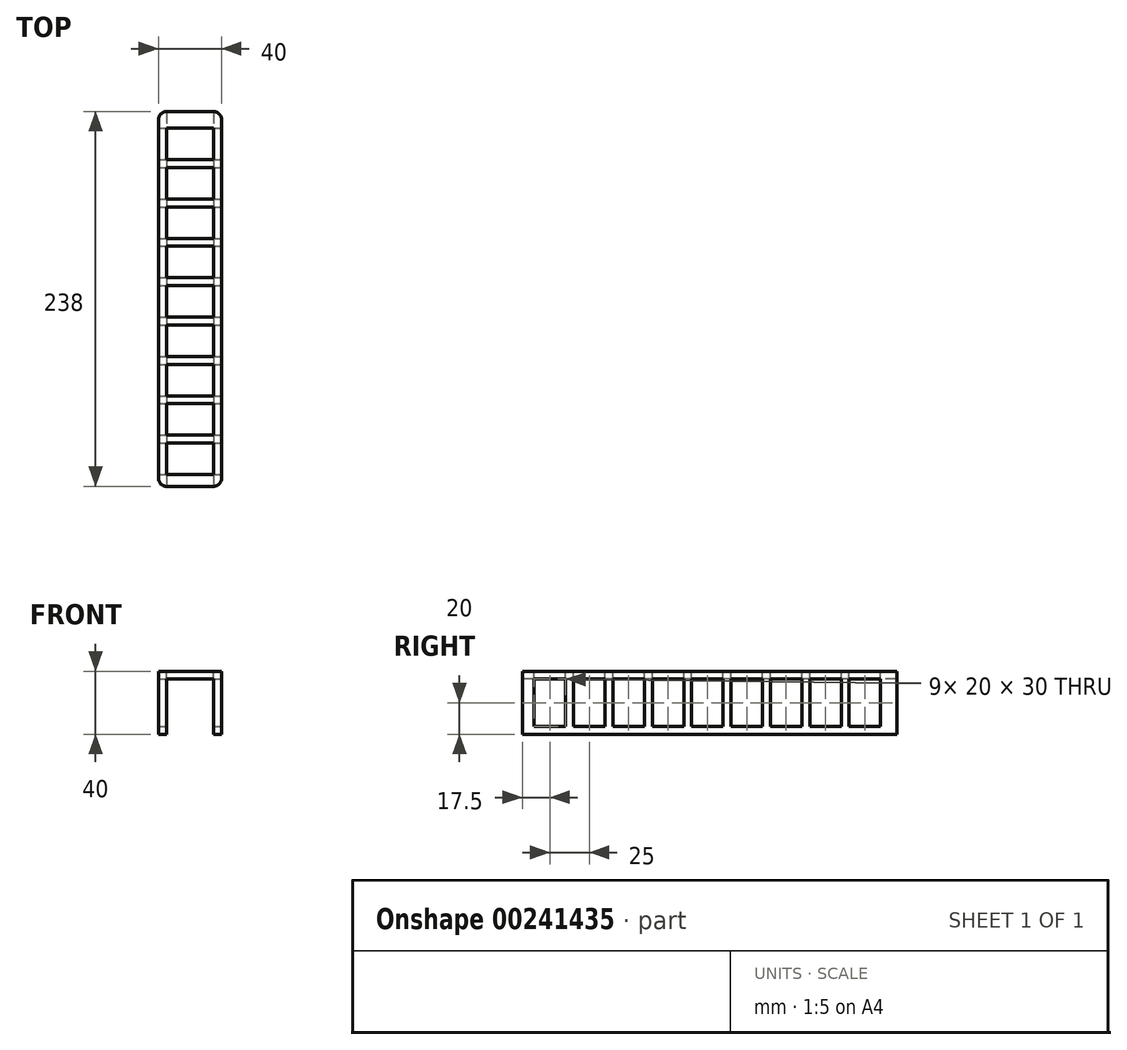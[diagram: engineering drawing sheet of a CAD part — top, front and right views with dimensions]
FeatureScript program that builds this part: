
annotation { "Feature Type Name" : "Feature", "Feature Type Description" : "" }
export const myFeature = defineFeature(function(context is Context, id is Id, definition is map)
    precondition{}
    {
        {
            var Q0;
            Q0=qCreatedBy(makeId("Top.planeOp"),FACE);
            var sketch = newSketch(context, id + "F0", { "sketchPlane" : qUnion([Q0])});
            skLineSegment(sketch, "E0.bottom", {"start": v(-17.49, 119) * mm, "end": v(22.51, 119) * mm});
            skLineSegment(sketch, "E0.top", {"start": v(-17.49, -119) * mm, "end": v(22.51, -119) * mm});
            skLineSegment(sketch, "E0.left", {"start": v(-17.49, 119) * mm, "end": v(-17.49, -119) * mm});
            skLineSegment(sketch, "E0.right", {"start": v(22.51, 119) * mm, "end": v(22.51, -119) * mm});
            skPoint(sketch, "E0.middle", {"position": v(2.51, 0) * mm});
            skSolve(sketch);
        }
        {
            var Q0;
            Q0 = qSketchRegion(id + "F0", true);
            extrude(context, id + "F1", {"entities" : qUnion([Q0]), "depth" : 40 * mm});
        }
        {
            var Q0;
            Q0=makeQuery(id+"F1.opExtrude","SWEPT_EDGE",EDGE,{"disambiguationData":[OSD([sQuery(id+"F0.wireOp",EDGE,"E0.top"),sQuery(id+"F0.wireOp",EDGE,"E0.right")])]});
            var Q1;
            Q1=makeQuery(id+"F1.opExtrude","SWEPT_EDGE",EDGE,{"disambiguationData":[OSD([sQuery(id+"F0.wireOp",EDGE,"E0.top"),sQuery(id+"F0.wireOp",EDGE,"E0.left")])]});
            var Q2;
            Q2=makeQuery(id+"F1.opExtrude","SWEPT_EDGE",EDGE,{"disambiguationData":[OSD([sQuery(id+"F0.wireOp",EDGE,"E0.bottom"),sQuery(id+"F0.wireOp",EDGE,"E0.right")])]});
            var Q3;
            Q3=makeQuery(id+"F1.opExtrude","SWEPT_EDGE",EDGE,{"disambiguationData":[OSD([sQuery(id+"F0.wireOp",EDGE,"E0.bottom"),sQuery(id+"F0.wireOp",EDGE,"E0.left")])]});
            fillet(context, id + "F2", {"entities" : qUnion([Q0, Q1, Q2, Q3]), "radius" : 5 * mm, "tangentPropagation" : true, "allowEdgeOverflow" : false});
        }
        {
            var Q0;
            Q0=makeQuery(id+"F1.opExtrude","SWEPT_FACE",FACE,{"disambiguationData":[OSD([sQuery(id+"F0.wireOp",EDGE,"E0.top")])]});
            var sketch = newSketch(context, id + "F3", { "sketchPlane" : qUnion([Q0])});
            skLineSegment(sketch, "E1.bottom", {"start": v(17.51, 0) * mm, "end": v(-12.49, 0) * mm});
            skLineSegment(sketch, "E1.top", {"start": v(17.51, 35) * mm, "end": v(-12.49, 35) * mm});
            skLineSegment(sketch, "E1.left", {"start": v(17.51, 0) * mm, "end": v(17.51, 35) * mm});
            skLineSegment(sketch, "E1.right", {"start": v(-12.49, 0) * mm, "end": v(-12.49, 35) * mm});
            skSolve(sketch);
        }
        {
            var Q0;
            Q0 = qSketchRegion(id + "F3", true);
            extrude(context, id + "F4", {"entities" : qUnion([Q0]), "operationType" : NewBodyOperationType.REMOVE, "endBound" : BoundingType.THROUGH_ALL, "oppositeDirection" : true, "depth" : 25 * mm});
        }
        {
            var Q0;
            Q0=makeQuery(id+"F1.opExtrude","SWEPT_FACE",FACE,{"disambiguationData":[OSD([sQuery(id+"F0.wireOp",EDGE,"E0.right")])]});
            var sketch = newSketch(context, id + "F5", { "sketchPlane" : qUnion([Q0])});
            skLineSegment(sketch, "E2.bottom", {"start": v(-111.5, 5) * mm, "end": v(-91.5, 5) * mm});
            skLineSegment(sketch, "E2.top", {"start": v(-111.5, 35) * mm, "end": v(-91.5, 35) * mm});
            skLineSegment(sketch, "E2.left", {"start": v(-111.5, 5) * mm, "end": v(-111.5, 35) * mm});
            skLineSegment(sketch, "E2.right", {"start": v(-91.5, 5) * mm, "end": v(-91.5, 35) * mm});
            skLineSegment(sketch, "E3.1.0.0", {"start": v(-86.5, 35) * mm, "end": v(-66.5, 35) * mm});
            skLineSegment(sketch, "E3.1.0.1", {"start": v(-86.5, 5) * mm, "end": v(-86.5, 35) * mm});
            skLineSegment(sketch, "E3.1.0.2", {"start": v(-86.5, 5) * mm, "end": v(-66.5, 5) * mm});
            skLineSegment(sketch, "E3.1.0.3", {"start": v(-66.5, 5) * mm, "end": v(-66.5, 35) * mm});
            skLineSegment(sketch, "E3.2.0.0", {"start": v(-61.5, 35) * mm, "end": v(-41.5, 35) * mm});
            skLineSegment(sketch, "E3.2.0.1", {"start": v(-61.5, 5) * mm, "end": v(-61.5, 35) * mm});
            skLineSegment(sketch, "E3.2.0.2", {"start": v(-61.5, 5) * mm, "end": v(-41.5, 5) * mm});
            skLineSegment(sketch, "E3.2.0.3", {"start": v(-41.5, 5) * mm, "end": v(-41.5, 35) * mm});
            skLineSegment(sketch, "E3.3.0.0", {"start": v(-36.5, 35) * mm, "end": v(-16.5, 35) * mm});
            skLineSegment(sketch, "E3.3.0.1", {"start": v(-36.5, 5) * mm, "end": v(-36.5, 35) * mm});
            skLineSegment(sketch, "E3.3.0.2", {"start": v(-36.5, 5) * mm, "end": v(-16.5, 5) * mm});
            skLineSegment(sketch, "E3.3.0.3", {"start": v(-16.5, 5) * mm, "end": v(-16.5, 35) * mm});
            skLineSegment(sketch, "E3.4.0.0", {"start": v(-11.5, 35) * mm, "end": v(8.5, 35) * mm});
            skLineSegment(sketch, "E3.4.0.1", {"start": v(-11.5, 5) * mm, "end": v(-11.5, 35) * mm});
            skLineSegment(sketch, "E3.4.0.2", {"start": v(-11.5, 5) * mm, "end": v(8.5, 5) * mm});
            skLineSegment(sketch, "E3.4.0.3", {"start": v(8.5, 5) * mm, "end": v(8.5, 35) * mm});
            skLineSegment(sketch, "E3.5.0.0", {"start": v(13.5, 35) * mm, "end": v(33.5, 35) * mm});
            skLineSegment(sketch, "E3.5.0.1", {"start": v(13.5, 5) * mm, "end": v(13.5, 35) * mm});
            skLineSegment(sketch, "E3.5.0.2", {"start": v(13.5, 5) * mm, "end": v(33.5, 5) * mm});
            skLineSegment(sketch, "E3.5.0.3", {"start": v(33.5, 5) * mm, "end": v(33.5, 35) * mm});
            skLineSegment(sketch, "E3.6.0.0", {"start": v(38.5, 35) * mm, "end": v(58.5, 35) * mm});
            skLineSegment(sketch, "E3.6.0.1", {"start": v(38.5, 5) * mm, "end": v(38.5, 35) * mm});
            skLineSegment(sketch, "E3.6.0.2", {"start": v(38.5, 5) * mm, "end": v(58.5, 5) * mm});
            skLineSegment(sketch, "E3.6.0.3", {"start": v(58.5, 5) * mm, "end": v(58.5, 35) * mm});
            skLineSegment(sketch, "E3.7.0.0", {"start": v(63.5, 35) * mm, "end": v(83.5, 35) * mm});
            skLineSegment(sketch, "E3.7.0.1", {"start": v(63.5, 5) * mm, "end": v(63.5, 35) * mm});
            skLineSegment(sketch, "E3.7.0.2", {"start": v(63.5, 5) * mm, "end": v(83.5, 5) * mm});
            skLineSegment(sketch, "E3.7.0.3", {"start": v(83.5, 5) * mm, "end": v(83.5, 35) * mm});
            skLineSegment(sketch, "E3.8.0.0", {"start": v(88.5, 35) * mm, "end": v(108.5, 35) * mm});
            skLineSegment(sketch, "E3.8.0.1", {"start": v(88.5, 5) * mm, "end": v(88.5, 35) * mm});
            skLineSegment(sketch, "E3.8.0.2", {"start": v(88.5, 5) * mm, "end": v(108.5, 5) * mm});
            skLineSegment(sketch, "E3.8.0.3", {"start": v(108.5, 5) * mm, "end": v(108.5, 35) * mm});
            skLineSegment(sketch, "E3.direction1", {"start": v(-111.5, 35) * mm, "end": v(-86.5, 35) * mm, "construction": true});
            skSolve(sketch);
        }
        {
            var Q0;
            Q0 = qSketchRegion(id + "F5", true);
            extrude(context, id + "F6", {"entities" : qUnion([Q0]), "operationType" : NewBodyOperationType.REMOVE, "endBound" : BoundingType.THROUGH_ALL, "oppositeDirection" : true, "depth" : 25 * mm});
        }
        {
            var Q0;
            Q0=makeQuery(id+"F1.opExtrude","CAP_FACE",FACE,{"disambiguationData":[OSD([sQuery(id+"F0.wireOp",EDGE,"E0.bottom"),sQuery(id+"F0.wireOp",EDGE,"E0.top"),sQuery(id+"F0.wireOp",EDGE,"E0.left"),sQuery(id+"F0.wireOp",EDGE,"E0.right")])],"isStart":false});
            var sketch = newSketch(context, id + "F7", { "sketchPlane" : qUnion([Q0])});
            skLineSegment(sketch, "E4.bottom", {"start": v(-12.49, -111.5) * mm, "end": v(17.51, -111.5) * mm});
            skLineSegment(sketch, "E4.top", {"start": v(-12.49, -91.5) * mm, "end": v(17.51, -91.5) * mm});
            skLineSegment(sketch, "E4.left", {"start": v(-12.49, -111.5) * mm, "end": v(-12.49, -91.5) * mm});
            skLineSegment(sketch, "E4.right", {"start": v(17.51, -111.5) * mm, "end": v(17.51, -91.5) * mm});
            skLineSegment(sketch, "E5.0.1.0", {"start": v(-12.49, -86.5) * mm, "end": v(17.51, -86.5) * mm});
            skLineSegment(sketch, "E5.0.1.1", {"start": v(-12.49, -66.5) * mm, "end": v(17.51, -66.5) * mm});
            skLineSegment(sketch, "E5.0.1.2", {"start": v(-12.49, -86.5) * mm, "end": v(-12.49, -66.5) * mm});
            skLineSegment(sketch, "E5.0.1.3", {"start": v(17.51, -86.5) * mm, "end": v(17.51, -66.5) * mm});
            skLineSegment(sketch, "E5.0.2.0", {"start": v(-12.49, -61.5) * mm, "end": v(17.51, -61.5) * mm});
            skLineSegment(sketch, "E5.0.2.1", {"start": v(-12.49, -41.5) * mm, "end": v(17.51, -41.5) * mm});
            skLineSegment(sketch, "E5.0.2.2", {"start": v(-12.49, -61.5) * mm, "end": v(-12.49, -41.5) * mm});
            skLineSegment(sketch, "E5.0.2.3", {"start": v(17.51, -61.5) * mm, "end": v(17.51, -41.5) * mm});
            skLineSegment(sketch, "E5.0.3.0", {"start": v(-12.49, -36.5) * mm, "end": v(17.51, -36.5) * mm});
            skLineSegment(sketch, "E5.0.3.1", {"start": v(-12.49, -16.5) * mm, "end": v(17.51, -16.5) * mm});
            skLineSegment(sketch, "E5.0.3.2", {"start": v(-12.49, -36.5) * mm, "end": v(-12.49, -16.5) * mm});
            skLineSegment(sketch, "E5.0.3.3", {"start": v(17.51, -36.5) * mm, "end": v(17.51, -16.5) * mm});
            skLineSegment(sketch, "E5.0.4.0", {"start": v(-12.49, -11.5) * mm, "end": v(17.51, -11.5) * mm});
            skLineSegment(sketch, "E5.0.4.1", {"start": v(-12.49, 8.5) * mm, "end": v(17.51, 8.5) * mm});
            skLineSegment(sketch, "E5.0.4.2", {"start": v(-12.49, -11.5) * mm, "end": v(-12.49, 8.5) * mm});
            skLineSegment(sketch, "E5.0.4.3", {"start": v(17.51, -11.5) * mm, "end": v(17.51, 8.5) * mm});
            skLineSegment(sketch, "E5.0.5.0", {"start": v(-12.49, 13.5) * mm, "end": v(17.51, 13.5) * mm});
            skLineSegment(sketch, "E5.0.5.1", {"start": v(-12.49, 33.5) * mm, "end": v(17.51, 33.5) * mm});
            skLineSegment(sketch, "E5.0.5.2", {"start": v(-12.49, 13.5) * mm, "end": v(-12.49, 33.5) * mm});
            skLineSegment(sketch, "E5.0.5.3", {"start": v(17.51, 13.5) * mm, "end": v(17.51, 33.5) * mm});
            skLineSegment(sketch, "E5.0.6.0", {"start": v(-12.49, 38.5) * mm, "end": v(17.51, 38.5) * mm});
            skLineSegment(sketch, "E5.0.6.1", {"start": v(-12.49, 58.5) * mm, "end": v(17.51, 58.5) * mm});
            skLineSegment(sketch, "E5.0.6.2", {"start": v(-12.49, 38.5) * mm, "end": v(-12.49, 58.5) * mm});
            skLineSegment(sketch, "E5.0.6.3", {"start": v(17.51, 38.5) * mm, "end": v(17.51, 58.5) * mm});
            skLineSegment(sketch, "E5.0.7.0", {"start": v(-12.49, 63.5) * mm, "end": v(17.51, 63.5) * mm});
            skLineSegment(sketch, "E5.0.7.1", {"start": v(-12.49, 83.5) * mm, "end": v(17.51, 83.5) * mm});
            skLineSegment(sketch, "E5.0.7.2", {"start": v(-12.49, 63.5) * mm, "end": v(-12.49, 83.5) * mm});
            skLineSegment(sketch, "E5.0.7.3", {"start": v(17.51, 63.5) * mm, "end": v(17.51, 83.5) * mm});
            skLineSegment(sketch, "E5.0.8.0", {"start": v(-12.49, 88.5) * mm, "end": v(17.51, 88.5) * mm});
            skLineSegment(sketch, "E5.0.8.1", {"start": v(-12.49, 108.5) * mm, "end": v(17.51, 108.5) * mm});
            skLineSegment(sketch, "E5.0.8.2", {"start": v(-12.49, 88.5) * mm, "end": v(-12.49, 108.5) * mm});
            skLineSegment(sketch, "E5.0.8.3", {"start": v(17.51, 88.5) * mm, "end": v(17.51, 108.5) * mm});
            skLineSegment(sketch, "E5.direction1", {"start": v(-12.49, -111.5) * mm, "end": v(12.51, -111.5) * mm, "construction": true});
            skLineSegment(sketch, "E5.direction2", {"start": v(-12.49, -111.5) * mm, "end": v(-12.49, -86.5) * mm, "construction": true});
            skSolve(sketch);
        }
        {
            var Q0;
            Q0 = qSketchRegion(id + "F7", true);
            extrude(context, id + "F8", {"entities" : qUnion([Q0]), "operationType" : NewBodyOperationType.REMOVE, "endBound" : BoundingType.THROUGH_ALL, "oppositeDirection" : true, "depth" : 25 * mm});
        }
    });
